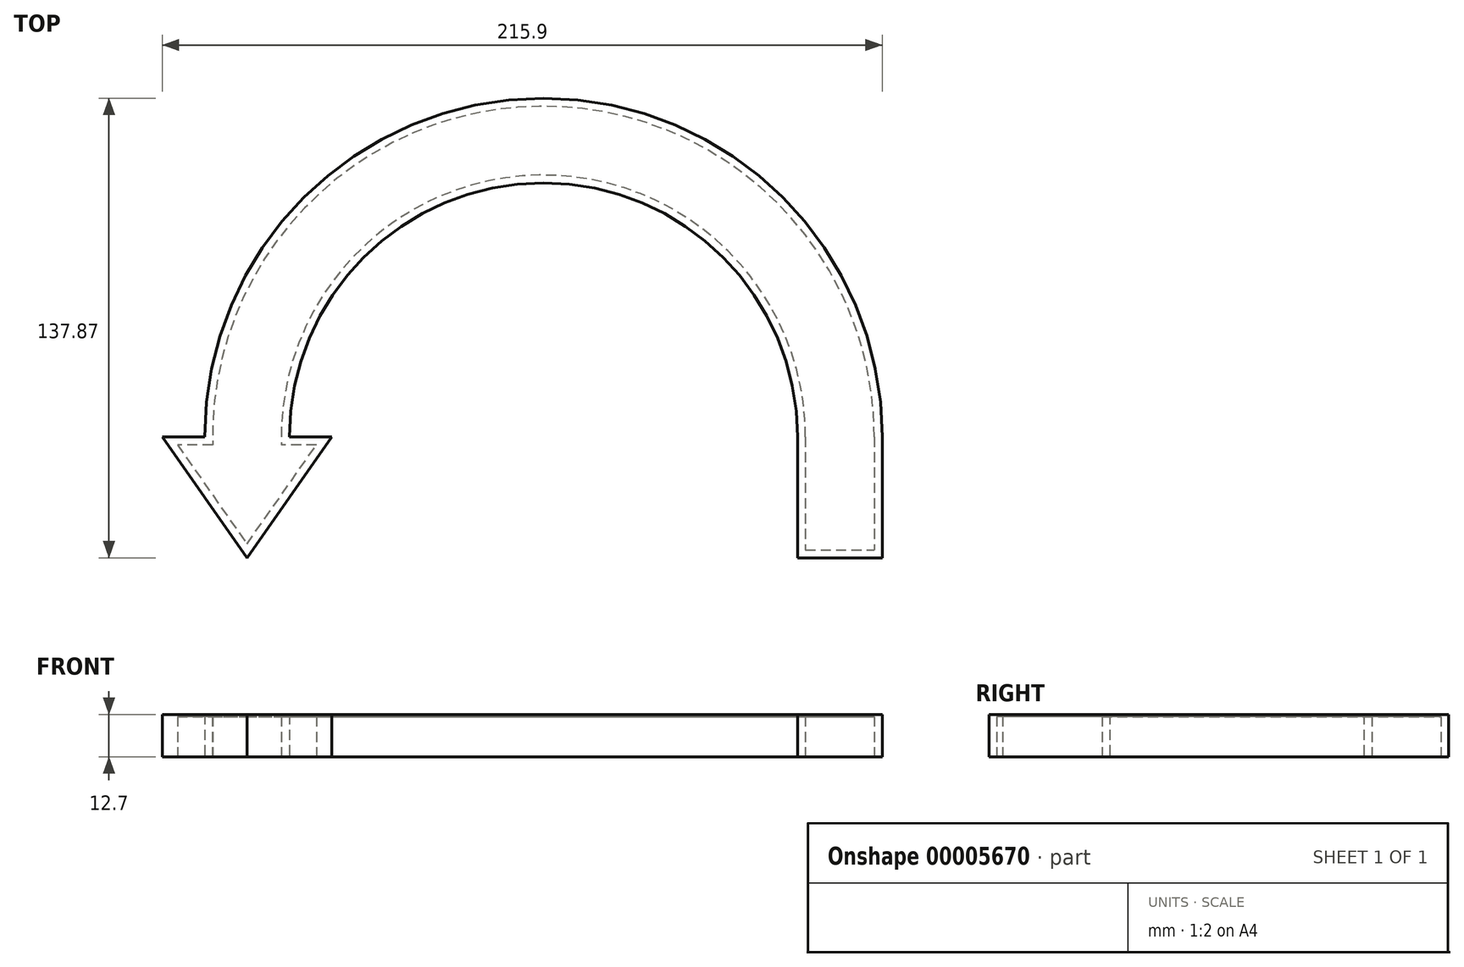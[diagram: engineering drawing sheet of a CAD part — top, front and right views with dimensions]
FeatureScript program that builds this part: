
annotation { "Feature Type Name" : "Feature", "Feature Type Description" : "" }
export const myFeature = defineFeature(function(context is Context, id is Id, definition is map)
    precondition{}
    {
        {
            var Q0;
            Q0=qCreatedBy(makeId("Top.planeOp"),FACE);
            var sketch = newSketch(context, id + "F0", { "sketchPlane" : qUnion([Q0])});
            skArc(sketch, "E0", {"start": v(101.6, 0) * mm, "mid": v(0, 101.6) * mm, "end": v(-101.6, 0) * mm});
            skArc(sketch, "E1", {"start": v(76.2, 0) * mm, "mid": v(0, 76.2) * mm, "end": v(-76.2, 0) * mm});
            skCircle(sketch, "E2", {"center": v(0, 0) * mm, "radius": 88.9 * mm, "construction": true});
            skLineSegment(sketch, "E3", {"start": v(-63.5, 0) * mm, "end": v(-76.2, 0) * mm});
            skLineSegment(sketch, "E4", {"start": v(-114.3, 0) * mm, "end": v(-88.9, -36.27) * mm});
            skLineSegment(sketch, "E5", {"start": v(-88.9, -36.27) * mm, "end": v(-63.5, 0) * mm});
            skLineSegment(sketch, "E6.trimOffspring", {"start": v(-101.6, 0) * mm, "end": v(-114.3, 0) * mm});
            skLineSegment(sketch, "E7.top", {"start": v(76.2, -36.27) * mm, "end": v(101.6, -36.27) * mm});
            skLineSegment(sketch, "E7.left", {"start": v(76.2, 0) * mm, "end": v(76.2, -36.27) * mm});
            skLineSegment(sketch, "E7.right", {"start": v(101.6, 0) * mm, "end": v(101.6, -36.27) * mm});
            skSolve(sketch);
        }
        {
            var Q0;
            Q0 = qSketchRegion(id + "F0", true);
            extrude(context, id + "F1", {"entities" : qUnion([Q0]), "depth" : 12.7 * mm});
        }
        {
            var Q0;
            Q0=makeQuery(id+"F1.opExtrude","CAP_FACE",FACE,{"disambiguationData":[OSD([sQuery(id+"F0.wireOp",EDGE,"E0"),sQuery(id+"F0.wireOp",EDGE,"E1"),sQuery(id+"F0.wireOp",EDGE,"E3"),sQuery(id+"F0.wireOp",EDGE,"E4"),sQuery(id+"F0.wireOp",EDGE,"E5"),sQuery(id+"F0.wireOp",EDGE,"E6.trimOffspring"),sQuery(id+"F0.wireOp",EDGE,"E7.top"),sQuery(id+"F0.wireOp",EDGE,"E7.left"),sQuery(id+"F0.wireOp",EDGE,"E7.right")])],"isStart":true});
            var sketch = newSketch(context, id + "F2", { "sketchPlane" : qUnion([Q0])});
            skLineSegment(sketch, "E8.0", {"start": v(-109.74, 2.38) * mm, "end": v(-88.9, 32.13) * mm});
            skLineSegment(sketch, "E8.1", {"start": v(-99.2, 2.38) * mm, "end": v(-109.74, 2.38) * mm});
            skArc(sketch, "E8.2", {"start": v(99.22, 0) * mm, "mid": v(-1.19, -99.22) * mm, "end": v(-99.2, 2.38) * mm});
            skLineSegment(sketch, "E8.3", {"start": v(99.22, 0) * mm, "end": v(99.22, 33.9) * mm});
            skLineSegment(sketch, "E8.4", {"start": v(78.58, 33.9) * mm, "end": v(99.22, 33.9) * mm});
            skLineSegment(sketch, "E8.5", {"start": v(-88.9, 32.13) * mm, "end": v(-68.06, 2.38) * mm});
            skLineSegment(sketch, "E8.6", {"start": v(78.58, 0) * mm, "end": v(78.58, 33.9) * mm});
            skArc(sketch, "E8.7", {"start": v(78.58, 0) * mm, "mid": v(-1.19, -78.57) * mm, "end": v(-78.54, 2.38) * mm});
            skLineSegment(sketch, "E8.8", {"start": v(-68.06, 2.38) * mm, "end": v(-78.54, 2.38) * mm});
            skSolve(sketch);
        }
        {
            var Q0;
            Q0=makeQuery(id+"F2.imprint","IMPRINT",FACE,{"disambiguationData":[TD([[makeQuery(id+"F2.imprint","IMPRINT",EDGE,{"derivedFrom":sQuery(id+"F2.wireOp",EDGE,"E8.0")}),-1.0]])]});
            extrude(context, id + "F3", {"entities" : qUnion([Q0]), "operationType" : NewBodyOperationType.REMOVE, "oppositeDirection" : true, "depth" : 12.06 * mm});
        }
    });
